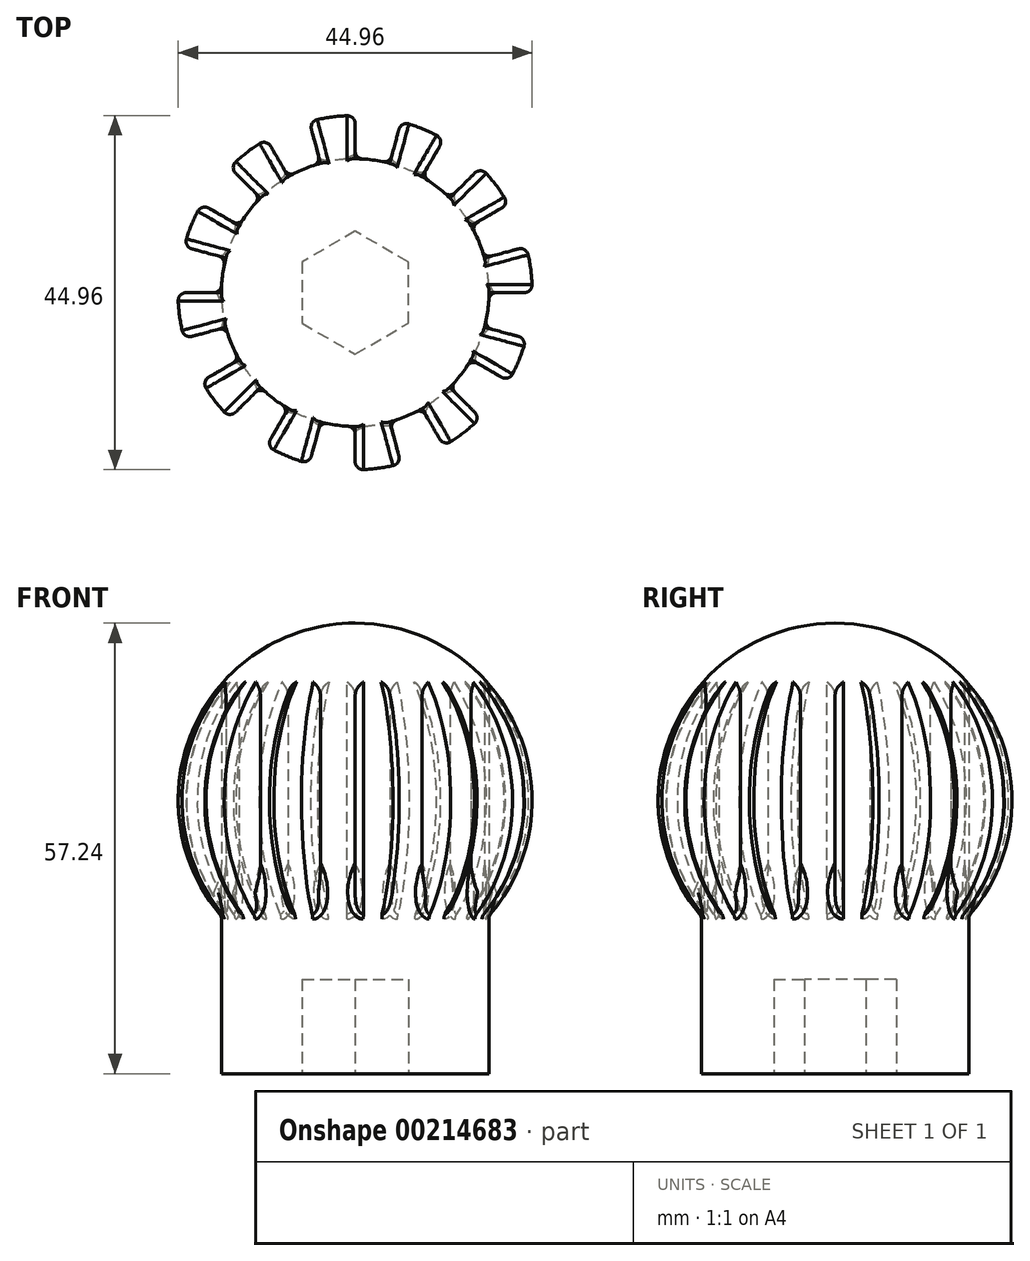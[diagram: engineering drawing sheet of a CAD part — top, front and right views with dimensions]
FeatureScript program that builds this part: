
annotation { "Feature Type Name" : "Feature", "Feature Type Description" : "" }
export const myFeature = defineFeature(function(context is Context, id is Id, definition is map)
    precondition{}
    {
        {
            var Q0;
            Q0=qCreatedBy(makeId("Front.planeOp"),FACE);
            var sketch = newSketch(context, id + "F0", { "sketchPlane" : qUnion([Q0])});
            skLineSegment(sketch, "E0", {"start": v(0, 0) * mm, "end": v(-17, 0) * mm});
            skLineSegment(sketch, "E1", {"start": v(-17, 0) * mm, "end": v(-17, 20) * mm});
            skCircle(sketch, "E2", {"center": v(0, 34.74) * mm, "radius": 22.5 * mm});
            skLineSegment(sketch, "E3", {"start": v(0, 0) * mm, "end": v(17, 0) * mm});
            skLineSegment(sketch, "E4", {"start": v(17, 0) * mm, "end": v(17, 20) * mm});
            skLineSegment(sketch, "E5", {"start": v(0, 0) * mm, "end": v(0, 57.24) * mm});
            skSolve(sketch);
        }
        {
            var Q0;
            {var subQ0=sQuery(id+"F0.wireOp",EDGE,"E2");var subQ1=makeQuery(id+"F0.imprint","INTERSECT",VERTEX,{"derivedFrom":[subQ0,sQuery(id+"F0.wireOp",EDGE,"E4")]});Q0=makeQuery(id+"F0.imprint","IMPRINT",FACE,{"disambiguationData":[TD([[makeQuery(id+"F0.imprint","IMPRINT",EDGE,{"disambiguationData":[TD([[subQ1,1.0]])],"derivedFrom":subQ0}),1.0]])]});}
            var Q1;
            Q1=sQuery(id+"F0.wireOp",EDGE,"E5");
            revolve(context, id + "F1", {"surfaceOperationType" : NewSurfaceOperationType.NEW, "entities" : qUnion([Q0]), "axis" : qUnion([Q1]), "revolveType" : RevolveType.FULL});
        }
        {
            var Q0;
            Q0=qCreatedBy(makeId("Top.planeOp"),FACE);
            var sketch = newSketch(context, id + "F2", { "sketchPlane" : qUnion([Q0])});
            skLineSegment(sketch, "E6", {"start": v(0, 0) * mm, "end": v(0, 22.5) * mm});
            skCircle(sketch, "E7", {"center": v(0, 0) * mm, "radius": 22.5 * mm});
            skLineSegment(sketch, "E8", {"start": v(0, 0) * mm, "end": v(5.82, 21.73) * mm});
            skCircle(sketch, "E9", {"center": v(0, 0) * mm, "radius": 17 * mm});
            skLineSegment(sketch, "E10.2.0", {"start": v(0, 0) * mm, "end": v(-5.82, 21.73) * mm});
            skLineSegment(sketch, "E10.3.0", {"start": v(0, 0) * mm, "end": v(-11.25, 19.49) * mm});
            skLineSegment(sketch, "E10.4.0", {"start": v(0, 0) * mm, "end": v(-15.9, 15.9) * mm});
            skLineSegment(sketch, "E10.5.0", {"start": v(0, 0) * mm, "end": v(-19.49, 11.25) * mm});
            skLineSegment(sketch, "E10.6.0", {"start": v(0, 0) * mm, "end": v(-21.73, 5.82) * mm});
            skLineSegment(sketch, "E10.7.0", {"start": v(0, 0) * mm, "end": v(-22.5, 0) * mm});
            skLineSegment(sketch, "E10.8.0", {"start": v(0, 0) * mm, "end": v(-21.73, -5.82) * mm});
            skLineSegment(sketch, "E10.9.0", {"start": v(0, 0) * mm, "end": v(-19.49, -11.25) * mm});
            skLineSegment(sketch, "E10.10.0", {"start": v(0, 0) * mm, "end": v(-15.9, -15.9) * mm});
            skLineSegment(sketch, "E10.11.0", {"start": v(0, 0) * mm, "end": v(-11.25, -19.49) * mm});
            skLineSegment(sketch, "E10.12.0", {"start": v(0, 0) * mm, "end": v(-5.82, -21.73) * mm});
            skLineSegment(sketch, "E10.13.0", {"start": v(0, 0) * mm, "end": v(0, -22.5) * mm});
            skLineSegment(sketch, "E10.14.0", {"start": v(0, 0) * mm, "end": v(5.82, -21.73) * mm});
            skLineSegment(sketch, "E10.15.0", {"start": v(0, 0) * mm, "end": v(11.25, -19.49) * mm});
            skLineSegment(sketch, "E10.16.0", {"start": v(0, 0) * mm, "end": v(15.9, -15.9) * mm});
            skLineSegment(sketch, "E10.17.0", {"start": v(0, 0) * mm, "end": v(19.49, -11.25) * mm});
            skLineSegment(sketch, "E10.18.0", {"start": v(0, 0) * mm, "end": v(21.73, -5.82) * mm});
            skLineSegment(sketch, "E10.19.0", {"start": v(0, 0) * mm, "end": v(22.5, 0) * mm});
            skLineSegment(sketch, "E10.20.0", {"start": v(0, 0) * mm, "end": v(21.73, 5.82) * mm});
            skLineSegment(sketch, "E10.21.0", {"start": v(0, 0) * mm, "end": v(19.49, 11.25) * mm});
            skLineSegment(sketch, "E10.22.0", {"start": v(0, 0) * mm, "end": v(15.9, 15.9) * mm});
            skLineSegment(sketch, "E10.23.0", {"start": v(0, 0) * mm, "end": v(11.25, 19.49) * mm});
            skSolve(sketch);
        }
        {
            var Q0;
            {var subQ0=sQuery(id+"F2.wireOp",EDGE,"E10.20.0");var subQ1=sQuery(id+"F2.wireOp",EDGE,"E7");var subQ2=makeQuery(id+"F2.imprint","INTERSECT",VERTEX,{"derivedFrom":[subQ1,subQ0]});Q0=makeQuery(id+"F2.imprint","IMPRINT",FACE,{"disambiguationData":[TD([[makeQuery(id+"F2.imprint","IMPRINT",EDGE,{"disambiguationData":[TD([[subQ2,-1.0]])],"derivedFrom":subQ1}),1.0]])]});}
            var Q1;
            {var subQ0=sQuery(id+"F2.wireOp",EDGE,"E10.22.0");var subQ1=sQuery(id+"F2.wireOp",EDGE,"E7");var subQ2=makeQuery(id+"F2.imprint","INTERSECT",VERTEX,{"derivedFrom":[subQ1,subQ0]});Q1=makeQuery(id+"F2.imprint","IMPRINT",FACE,{"disambiguationData":[TD([[makeQuery(id+"F2.imprint","IMPRINT",EDGE,{"disambiguationData":[TD([[subQ2,-1.0]])],"derivedFrom":subQ1}),1.0]])]});}
            var Q2;
            {var subQ0=sQuery(id+"F2.wireOp",EDGE,"E8");var subQ1=sQuery(id+"F2.wireOp",EDGE,"E7");var subQ2=makeQuery(id+"F2.imprint","INTERSECT",VERTEX,{"derivedFrom":[subQ1,subQ0]});Q2=makeQuery(id+"F2.imprint","IMPRINT",FACE,{"disambiguationData":[TD([[makeQuery(id+"F2.imprint","IMPRINT",EDGE,{"disambiguationData":[TD([[subQ2,-1.0]])],"derivedFrom":subQ1}),1.0]])]});}
            var Q3;
            {var subQ0=sQuery(id+"F2.wireOp",EDGE,"E10.2.0");var subQ1=sQuery(id+"F2.wireOp",EDGE,"E7");var subQ2=makeQuery(id+"F2.imprint","INTERSECT",VERTEX,{"derivedFrom":[subQ1,subQ0]});Q3=makeQuery(id+"F2.imprint","IMPRINT",FACE,{"disambiguationData":[TD([[makeQuery(id+"F2.imprint","IMPRINT",EDGE,{"disambiguationData":[TD([[subQ2,-1.0]])],"derivedFrom":subQ1}),1.0]])]});}
            var Q4;
            {var subQ0=sQuery(id+"F2.wireOp",EDGE,"E10.4.0");var subQ1=sQuery(id+"F2.wireOp",EDGE,"E7");var subQ2=makeQuery(id+"F2.imprint","INTERSECT",VERTEX,{"derivedFrom":[subQ1,subQ0]});Q4=makeQuery(id+"F2.imprint","IMPRINT",FACE,{"disambiguationData":[TD([[makeQuery(id+"F2.imprint","IMPRINT",EDGE,{"disambiguationData":[TD([[subQ2,-1.0]])],"derivedFrom":subQ1}),1.0]])]});}
            var Q5;
            {var subQ0=sQuery(id+"F2.wireOp",EDGE,"E10.6.0");var subQ1=sQuery(id+"F2.wireOp",EDGE,"E7");var subQ2=makeQuery(id+"F2.imprint","INTERSECT",VERTEX,{"derivedFrom":[subQ1,subQ0]});Q5=makeQuery(id+"F2.imprint","IMPRINT",FACE,{"disambiguationData":[TD([[makeQuery(id+"F2.imprint","IMPRINT",EDGE,{"disambiguationData":[TD([[subQ2,-1.0]])],"derivedFrom":subQ1}),1.0]])]});}
            var Q6;
            {var subQ0=sQuery(id+"F2.wireOp",EDGE,"E10.8.0");var subQ1=sQuery(id+"F2.wireOp",EDGE,"E7");var subQ2=makeQuery(id+"F2.imprint","INTERSECT",VERTEX,{"derivedFrom":[subQ1,subQ0]});Q6=makeQuery(id+"F2.imprint","IMPRINT",FACE,{"disambiguationData":[TD([[makeQuery(id+"F2.imprint","IMPRINT",EDGE,{"disambiguationData":[TD([[subQ2,-1.0]])],"derivedFrom":subQ1}),1.0]])]});}
            var Q7;
            {var subQ0=sQuery(id+"F2.wireOp",EDGE,"E10.10.0");var subQ1=sQuery(id+"F2.wireOp",EDGE,"E7");var subQ2=makeQuery(id+"F2.imprint","INTERSECT",VERTEX,{"derivedFrom":[subQ1,subQ0]});Q7=makeQuery(id+"F2.imprint","IMPRINT",FACE,{"disambiguationData":[TD([[makeQuery(id+"F2.imprint","IMPRINT",EDGE,{"disambiguationData":[TD([[subQ2,-1.0]])],"derivedFrom":subQ1}),1.0]])]});}
            var Q8;
            {var subQ0=sQuery(id+"F2.wireOp",EDGE,"E10.12.0");var subQ1=sQuery(id+"F2.wireOp",EDGE,"E7");var subQ2=makeQuery(id+"F2.imprint","INTERSECT",VERTEX,{"derivedFrom":[subQ1,subQ0]});Q8=makeQuery(id+"F2.imprint","IMPRINT",FACE,{"disambiguationData":[TD([[makeQuery(id+"F2.imprint","IMPRINT",EDGE,{"disambiguationData":[TD([[subQ2,-1.0]])],"derivedFrom":subQ1}),1.0]])]});}
            var Q9;
            {var subQ0=sQuery(id+"F2.wireOp",EDGE,"E10.14.0");var subQ1=sQuery(id+"F2.wireOp",EDGE,"E7");var subQ2=makeQuery(id+"F2.imprint","INTERSECT",VERTEX,{"derivedFrom":[subQ1,subQ0]});Q9=makeQuery(id+"F2.imprint","IMPRINT",FACE,{"disambiguationData":[TD([[makeQuery(id+"F2.imprint","IMPRINT",EDGE,{"disambiguationData":[TD([[subQ2,-1.0]])],"derivedFrom":subQ1}),1.0]])]});}
            var Q10;
            {var subQ0=sQuery(id+"F2.wireOp",EDGE,"E10.16.0");var subQ1=sQuery(id+"F2.wireOp",EDGE,"E7");var subQ2=makeQuery(id+"F2.imprint","INTERSECT",VERTEX,{"derivedFrom":[subQ1,subQ0]});Q10=makeQuery(id+"F2.imprint","IMPRINT",FACE,{"disambiguationData":[TD([[makeQuery(id+"F2.imprint","IMPRINT",EDGE,{"disambiguationData":[TD([[subQ2,-1.0]])],"derivedFrom":subQ1}),1.0]])]});}
            var Q11;
            {var subQ0=sQuery(id+"F2.wireOp",EDGE,"E10.18.0");var subQ1=sQuery(id+"F2.wireOp",EDGE,"E7");var subQ2=makeQuery(id+"F2.imprint","INTERSECT",VERTEX,{"derivedFrom":[subQ1,subQ0]});Q11=makeQuery(id+"F2.imprint","IMPRINT",FACE,{"disambiguationData":[TD([[makeQuery(id+"F2.imprint","IMPRINT",EDGE,{"disambiguationData":[TD([[subQ2,-1.0]])],"derivedFrom":subQ1}),1.0]])]});}
            extrude(context, id + "F3", {"entities" : qUnion([Q0, Q1, Q2, Q3, Q4, Q5, Q6, Q7, Q8, Q9, Q10, Q11]), "operationType" : NewBodyOperationType.REMOVE, "endBound" : BoundingType.THROUGH_ALL, "depth" : 25 * mm, "offsetDistance" : 25 * mm});
        }
        {
            var Q0;
            {var subQ0=sQuery(id+"F0.wireOp",EDGE,"E0");Q0=makeQuery(id+"F0.imprint","IMPRINT",FACE,{"disambiguationData":[TD([[makeQuery(id+"F0.imprint","IMPRINT",EDGE,{"derivedFrom":subQ0}),-1.0]])]});}
            var Q1;
            Q1=sQuery(id+"F0.wireOp",EDGE,"E5");
            revolve(context, id + "F4", {"operationType" : NewBodyOperationType.ADD, "surfaceOperationType" : NewSurfaceOperationType.NEW, "entities" : qUnion([Q0]), "axis" : qUnion([Q1]), "revolveType" : RevolveType.FULL});
        }
        {
            var Q0;
            Q0=makeQuery(id+"F4.opRevolve","SWEPT_FACE",FACE,{"disambiguationData":[OSD([sQuery(id+"F0.wireOp",EDGE,"E0")])]});
            var sketch = newSketch(context, id + "F5", { "sketchPlane" : qUnion([Q0])});
            skCircle(sketch, "E11.cCircle", {"center": v(0, 0) * mm, "radius": 6.75 * mm, "construction": true});
            skLineSegment(sketch, "E11.0", {"start": v(0, 7.8) * mm, "end": v(6.75, 3.9) * mm});
            skLineSegment(sketch, "E11.1", {"start": v(6.75, 3.9) * mm, "end": v(6.75, -3.9) * mm});
            skLineSegment(sketch, "E11.2", {"start": v(6.75, -3.9) * mm, "end": v(0, -7.8) * mm});
            skLineSegment(sketch, "E11.3", {"start": v(0, -7.8) * mm, "end": v(-6.75, -3.9) * mm});
            skLineSegment(sketch, "E11.4", {"start": v(-6.75, -3.9) * mm, "end": v(-6.75, 3.9) * mm});
            skLineSegment(sketch, "E11.5", {"start": v(-6.75, 3.9) * mm, "end": v(0, 7.8) * mm});
            skPoint(sketch, "E11.0.midPoint", {"position": v(3.37, 5.85) * mm});
            skSolve(sketch);
        }
        {
            var Q0;
            Q0=makeQuery(id+"F5.imprint","IMPRINT",FACE,{"disambiguationData":[TD([[makeQuery(id+"F5.imprint","IMPRINT",EDGE,{"derivedFrom":sQuery(id+"F5.wireOp",EDGE,"E11.0")}),-1.0]])]});
            extrude(context, id + "F6", {"entities" : qUnion([Q0]), "operationType" : NewBodyOperationType.REMOVE, "oppositeDirection" : true, "depth" : 12 * mm, "offsetDistance" : 25 * mm});
        }
        {
            var Q0;
            Q0=makeQuery(id+"F3.boolean.opBoolean","INTERSECT",EDGE,{"derivedFrom":[makeQuery(id+"F1.opRevolve","SWEPT_FACE",FACE,{"disambiguationData":[OSD([sQuery(id+"F0.wireOp",EDGE,"E2")])]}),makeQuery(id+"F3.opExtrude","SWEPT_FACE",FACE,{"disambiguationData":[OSD([sQuery(id+"F2.wireOp",EDGE,"E10.18.0")])]})]});
            var Q1;
            {var subQ0=sQuery(id+"F2.wireOp",EDGE,"E9");Q1=makeQuery(id+"F3.boolean.opBoolean","INTERSECT",EDGE,{"disambiguationData":[OD(1.0)],"derivedFrom":[makeQuery(id+"F1.opRevolve","SWEPT_FACE",FACE,{"disambiguationData":[OSD([sQuery(id+"F0.wireOp",EDGE,"E2")])]}),makeQuery(id+"F3.opExtrude","SWEPT_FACE",FACE,{"disambiguationData":[OSD([subQ0]),TDD([makeQuery(id+"F2.imprint","IMPRINT",EDGE,{"disambiguationData":[TD([[makeQuery(id+"F2.imprint","INTERSECT",VERTEX,{"derivedFrom":[subQ0,sQuery(id+"F2.wireOp",EDGE,"E10.19.0")]}),1.0]])],"derivedFrom":subQ0})])]})]});}
            var Q2;
            Q2=makeQuery(id+"F1.opRevolve","SWEPT_FACE",FACE,{"disambiguationData":[OSD([sQuery(id+"F0.wireOp",EDGE,"E2")])]});
            fillet(context, id + "F7", {"entities" : qUnion([Q0, Q1, Q2]), "tangentPropagation" : true, "radius" : 1 * mm, "defaultsChanged" : false, "vertexSettings" : [], "allowEdgeOverflow" : false});
        }
    });
